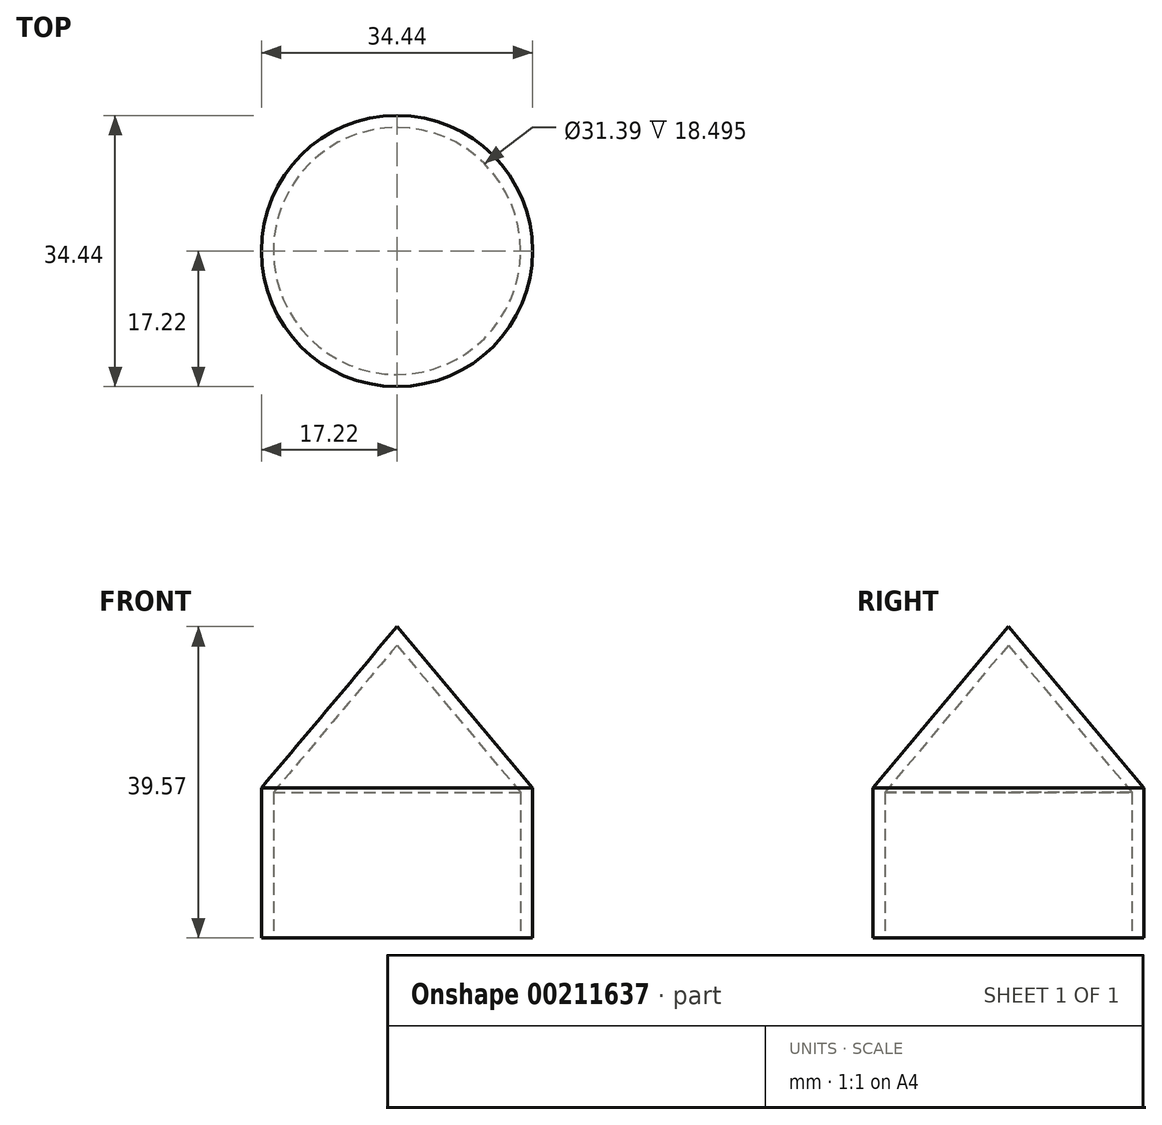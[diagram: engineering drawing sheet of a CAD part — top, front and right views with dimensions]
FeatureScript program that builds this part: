
annotation { "Feature Type Name" : "Feature", "Feature Type Description" : "" }
export const myFeature = defineFeature(function(context is Context, id is Id, definition is map)
    precondition{}
    {
        {
            var Q0;
            Q0=qCreatedBy(makeId("Front.planeOp"),FACE);
            var sketch = newSketch(context, id + "F0", { "sketchPlane" : qUnion([Q0])});
            skLineSegment(sketch, "E0", {"start": v(0, 0) * mm, "end": v(-17.22, 0) * mm, "construction": true});
            skLineSegment(sketch, "E1", {"start": v(-17.22, 0) * mm, "end": v(-17.22, 19.05) * mm});
            skLineSegment(sketch, "E2", {"start": v(-17.22, 19.05) * mm, "end": v(0, 39.57) * mm});
            skLineSegment(sketch, "E3.0", {"start": v(-15.7, 18.5) * mm, "end": v(0, 37.2) * mm});
            skLineSegment(sketch, "E3.1", {"start": v(-15.7, 0) * mm, "end": v(-15.7, 18.5) * mm});
            skLineSegment(sketch, "E4", {"start": v(-17.22, 0) * mm, "end": v(-15.7, 0) * mm});
            skLineSegment(sketch, "E5", {"start": v(0, 0) * mm, "end": v(0, 39.57) * mm, "construction": true});
            skLineSegment(sketch, "E6", {"start": v(0, 39.57) * mm, "end": v(0, 37.2) * mm});
            skSolve(sketch);
        }
        {
            var Q0;
            Q0=makeQuery(id+"F0.imprint","IMPRINT",FACE,{"disambiguationData":[TD([[makeQuery(id+"F0.imprint","IMPRINT",EDGE,{"derivedFrom":sQuery(id+"F0.wireOp",EDGE,"E1")}),-1.0]])]});
            var Q1;
            Q1=sQuery(id+"F0.wireOp",EDGE,"E5");
            revolve(context, id + "F1", {"entities" : qUnion([Q0]), "axis" : qUnion([Q1]), "revolveType" : RevolveType.FULL});
        }
    });
